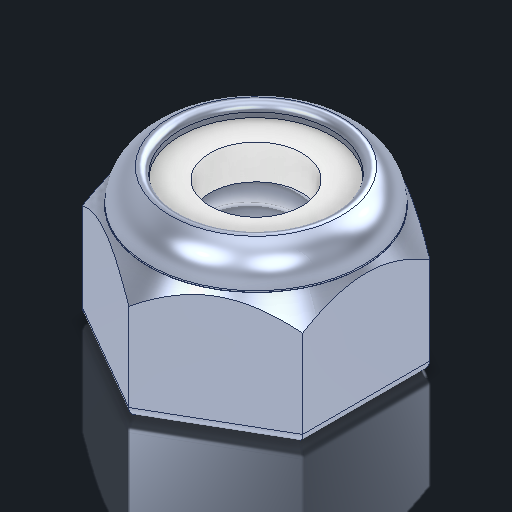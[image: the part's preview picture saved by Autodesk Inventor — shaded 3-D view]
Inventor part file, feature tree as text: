
AUTODESK INVENTOR PART (.ipt)
format: ipt  version: 2023.2 (Build 272271030, 271C)  size: 271,872 bytes
history: native  units: in
note: dims shown in document units (in); Inventor stores cm internally (conversion verified against a paired STEP export)
features: plane x2, other x1, imported_body x1, split x1, thread x1, extrude x1, fillet x1, sketch x1
ambient origin geometry x8: Origin, YZ Plane, XZ Plane, XY Plane, X Axis, Y Axis, Z Axis, Center Point
bodies: Body1 (feature_tree)
feature tree (9):
  parser-record x1  (decoder bookkeeping rows leaked as tree rows — omitted from the tree; the rows remain in map.json)
  imported_body  "Base1"
  plane  "Work Plane1"
  split  "Split1"
  thread  "Thread1"  [1 undecoded]
  plane  "Work Plane2"
  extrude  "Extrusion1"  Depth=0.015in TaperAngle=0.0deg
  fillet  "Fillet1"  Radius=0.015in
  sketch  "Sketch1"  dims[d2=-0.05in d4=0.053in d5=0.0in d6=0.015in]
note: 1 required parameter value undecoded (feature->parameter linkage not recoverable at this tier; creation-order binding heuristic only, values carry confidence <= 0.55)
